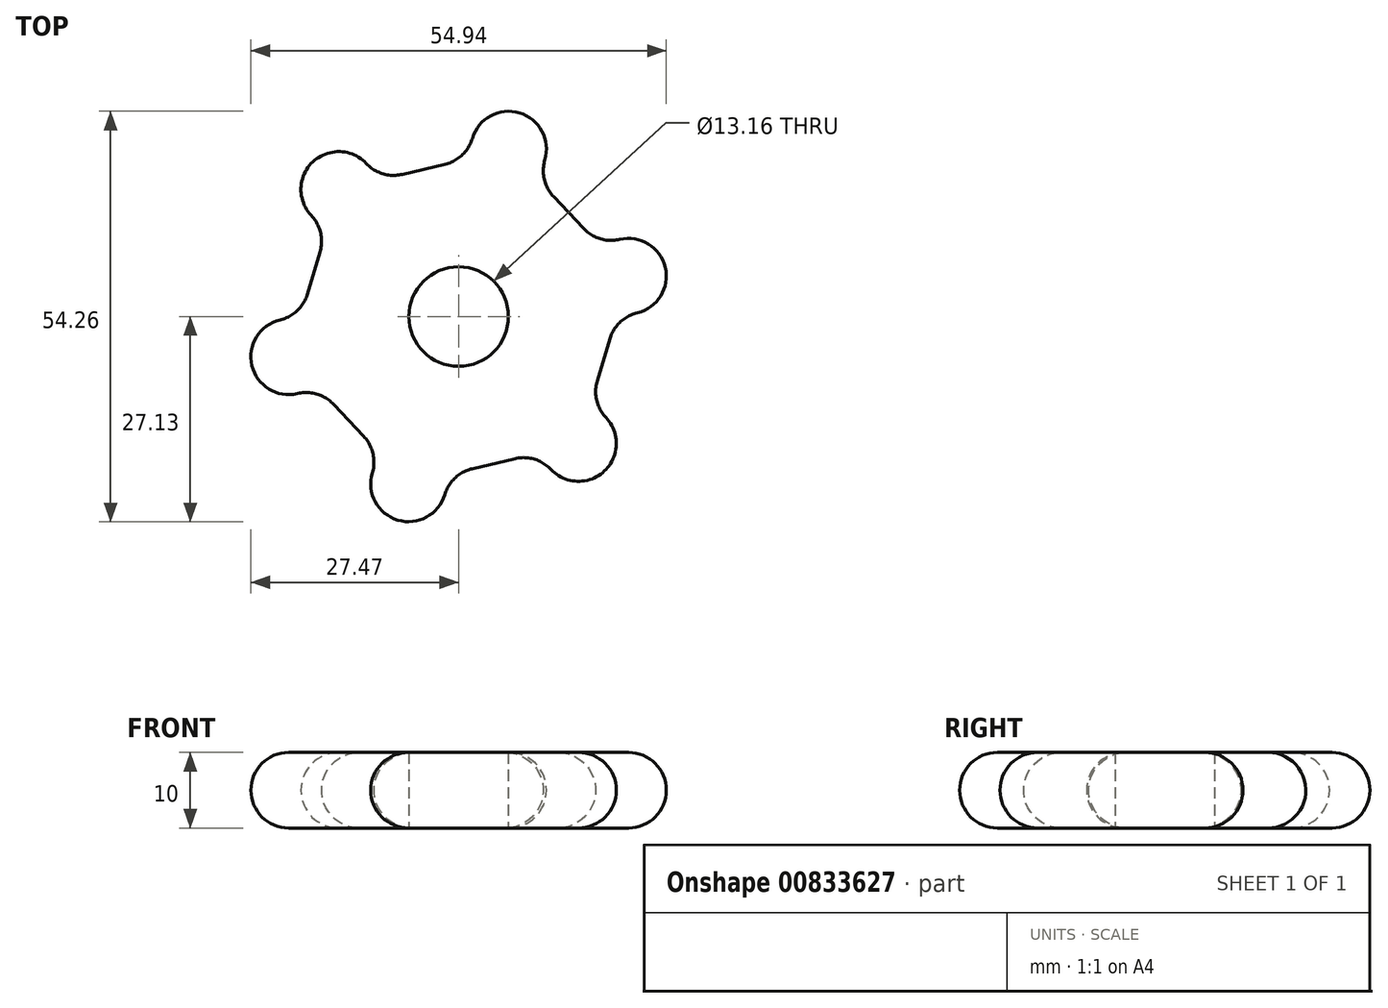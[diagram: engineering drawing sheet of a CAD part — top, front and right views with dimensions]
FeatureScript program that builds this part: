
annotation { "Feature Type Name" : "Feature", "Feature Type Description" : "" }
export const myFeature = defineFeature(function(context is Context, id is Id, definition is map)
    precondition{}
    {
        {
            var Q0;
            Q0=qCreatedBy(makeId("Top.planeOp"),FACE);
            var sketch = newSketch(context, id + "F0", { "sketchPlane" : qUnion([Q0])});
            skCircle(sketch, "E0", {"center": v(0, 0) * mm, "radius": 6.58 * mm});
            skLineSegment(sketch, "E1.0", {"start": v(-7.43, 18.8) * mm, "end": v(-1.8, 20.13) * mm});
            skLineSegment(sketch, "E1.1", {"start": v(12.56, 15.83) * mm, "end": v(16.53, 11.63) * mm});
            skLineSegment(sketch, "E1.2", {"start": v(19.99, -2.97) * mm, "end": v(18.33, -8.5) * mm});
            skLineSegment(sketch, "E1.3", {"start": v(7.43, -18.8) * mm, "end": v(1.8, -20.13) * mm});
            skLineSegment(sketch, "E1.4", {"start": v(-12.56, -15.83) * mm, "end": v(-16.53, -11.63) * mm});
            skLineSegment(sketch, "E1.5", {"start": v(-19.99, 2.97) * mm, "end": v(-18.33, 8.5) * mm});
            skPoint(sketch, "E1.0.midPoint", {"position": v(-4.62, 19.46) * mm});
            skArc(sketch, "E2", {"start": v(11.4, 20.7) * mm, "mid": v(8.05, 26.92) * mm, "end": v(1.83, 23.56) * mm});
            skArc(sketch, "E3", {"start": v(23.62, 0.47) * mm, "mid": v(27.33, 6.49) * mm, "end": v(21.32, 10.2) * mm});
            skArc(sketch, "E4", {"start": v(12.22, -20.23) * mm, "mid": v(19.28, -20.43) * mm, "end": v(19.49, -13.36) * mm});
            skArc(sketch, "E5", {"start": v(-11.4, -20.7) * mm, "mid": v(-8.05, -26.92) * mm, "end": v(-1.83, -23.56) * mm});
            skArc(sketch, "E6", {"start": v(-23.62, -0.47) * mm, "mid": v(-27.33, -6.49) * mm, "end": v(-21.32, -10.2) * mm});
            skArc(sketch, "E7", {"start": v(-12.22, 20.23) * mm, "mid": v(-19.28, 20.43) * mm, "end": v(-19.49, 13.36) * mm});
            skPoint(sketch, "E8.visualSharp", {"position": v(-17.29, 12) * mm});
            skArc(sketch, "E8.filletArc", {"start": v(-18.33, 8.5) * mm, "mid": v(-18.26, 11.08) * mm, "end": v(-19.49, 13.36) * mm});
            skPoint(sketch, "E9.visualSharp", {"position": v(-21.04, -0.54) * mm});
            skArc(sketch, "E9.filletArc", {"start": v(-23.62, -0.47) * mm, "mid": v(-21.35, 0.76) * mm, "end": v(-19.99, 2.97) * mm});
            skPoint(sketch, "E10.visualSharp", {"position": v(-19.04, -8.97) * mm});
            skArc(sketch, "E10.filletArc", {"start": v(-16.53, -11.63) * mm, "mid": v(-18.73, -10.27) * mm, "end": v(-21.32, -10.2) * mm});
            skPoint(sketch, "E11.visualSharp", {"position": v(-10.05, -18.49) * mm});
            skArc(sketch, "E11.filletArc", {"start": v(-11.4, -20.7) * mm, "mid": v(-11.33, -18.1) * mm, "end": v(-12.56, -15.83) * mm});
            skPoint(sketch, "E12.visualSharp", {"position": v(10.99, -17.95) * mm});
            skArc(sketch, "E12.filletArc", {"start": v(12.22, -20.23) * mm, "mid": v(10.01, -18.87) * mm, "end": v(7.43, -18.8) * mm});
            skPoint(sketch, "E13.visualSharp", {"position": v(17.29, -12) * mm});
            skArc(sketch, "E13.filletArc", {"start": v(18.33, -8.5) * mm, "mid": v(18.26, -11.08) * mm, "end": v(19.49, -13.36) * mm});
            skPoint(sketch, "E14.visualSharp", {"position": v(-1.75, -20.97) * mm});
            skArc(sketch, "E14.filletArc", {"start": v(1.8, -20.13) * mm, "mid": v(-0.47, -21.36) * mm, "end": v(-1.83, -23.56) * mm});
            skPoint(sketch, "E15.visualSharp", {"position": v(21.04, 0.54) * mm});
            skArc(sketch, "E15.filletArc", {"start": v(23.62, 0.47) * mm, "mid": v(21.35, -0.76) * mm, "end": v(19.99, -2.97) * mm});
            skPoint(sketch, "E16.visualSharp", {"position": v(19.04, 8.97) * mm});
            skArc(sketch, "E16.filletArc", {"start": v(16.53, 11.63) * mm, "mid": v(18.73, 10.27) * mm, "end": v(21.32, 10.2) * mm});
            skPoint(sketch, "E17.visualSharp", {"position": v(10.05, 18.49) * mm});
            skArc(sketch, "E17.filletArc", {"start": v(11.4, 20.7) * mm, "mid": v(11.33, 18.1) * mm, "end": v(12.56, 15.83) * mm});
            skPoint(sketch, "E18.visualSharp", {"position": v(1.75, 20.97) * mm});
            skArc(sketch, "E18.filletArc", {"start": v(-1.8, 20.13) * mm, "mid": v(0.47, 21.36) * mm, "end": v(1.83, 23.56) * mm});
            skPoint(sketch, "E19.visualSharp", {"position": v(-10.99, 17.95) * mm});
            skArc(sketch, "E19.filletArc", {"start": v(-12.22, 20.23) * mm, "mid": v(-10.01, 18.87) * mm, "end": v(-7.43, 18.8) * mm});
            skSolve(sketch);
        }
        {
            var Q0;
            Q0=makeQuery(id+"F0.imprint","IMPRINT",FACE,{"disambiguationData":[TD([[makeQuery(id+"F0.imprint","IMPRINT",EDGE,{"derivedFrom":sQuery(id+"F0.wireOp",EDGE,"E0")}),-1.0]])]});
            extrude(context, id + "F1", {"entities" : qUnion([Q0]), "depth" : 10 * mm, "offsetDistance" : 25 * mm});
        }
        {
            var Q0;
            Q0=makeQuery(id+"F1.opExtrude","CAP_EDGE",EDGE,{"disambiguationData":[OSD([sQuery(id+"F0.wireOp",EDGE,"E7")])],"isStart":false});
            var Q1;
            Q1=makeQuery(id+"F1.opExtrude","CAP_EDGE",EDGE,{"disambiguationData":[OSD([sQuery(id+"F0.wireOp",EDGE,"E19.filletArc")])],"isStart":false});
            var Q2;
            Q2=makeQuery(id+"F1.opExtrude","CAP_EDGE",EDGE,{"disambiguationData":[OSD([sQuery(id+"F0.wireOp",EDGE,"E1.0")])],"isStart":false});
            fillet(context, id + "F2", {"entities" : qUnion([Q0, Q1, Q2]), "radius" : 5 * mm, "tangentPropagation" : true, "allowEdgeOverflow" : false});
        }
        {
            var Q0;
            Q0=makeQuery(id+"F1.opExtrude","CAP_EDGE",EDGE,{"disambiguationData":[OSD([sQuery(id+"F0.wireOp",EDGE,"E6")])],"isStart":true});
            fillet(context, id + "F3", {"entities" : qUnion([Q0]), "radius" : 5 * mm, "tangentPropagation" : true, "allowEdgeOverflow" : false});
        }
    });
